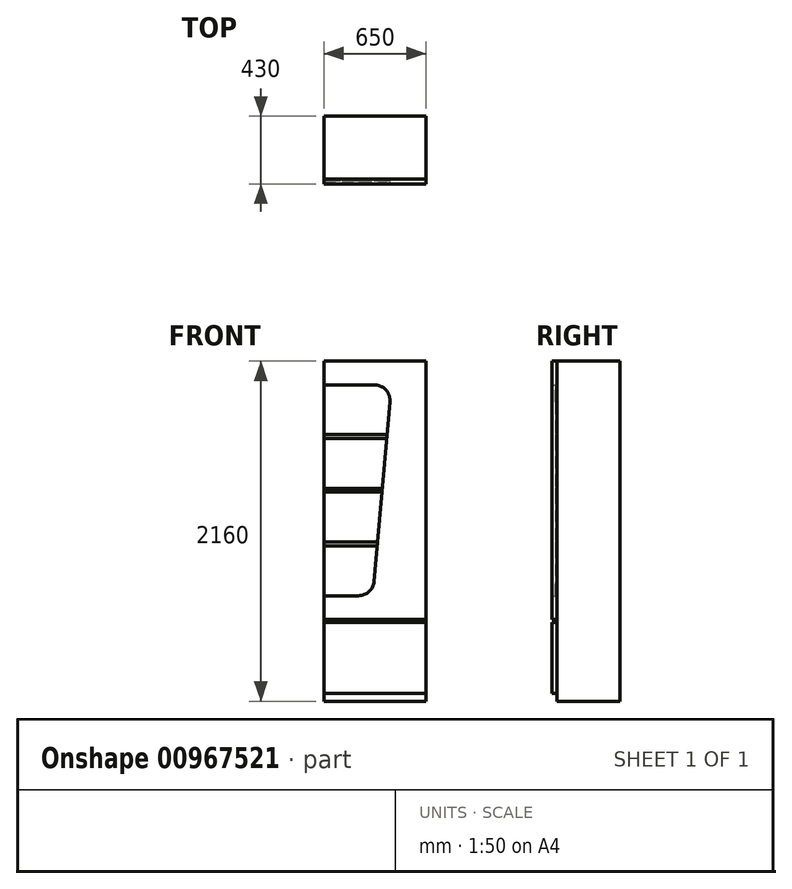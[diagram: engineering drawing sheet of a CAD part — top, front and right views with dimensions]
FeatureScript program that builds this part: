
annotation { "Feature Type Name" : "Feature", "Feature Type Description" : "" }
export const myFeature = defineFeature(function(context is Context, id is Id, definition is map)
    precondition{}
    {
        {
            assignVariable(context, id + "F0", {"variableType" : VariableType.LENGTH, "name" : "H", "lengthValue" : 2200 * mm});
        }
        {
            var Q0;
            Q0=qCreatedBy(makeId("Top.planeOp"),FACE);
            var sketch = newSketch(context, id + "F1", { "sketchPlane" : qUnion([Q0])});
            skLineSegment(sketch, "E0.bottom", {"start": v(0, 0) * mm, "end": v(650, 0) * mm});
            skLineSegment(sketch, "E0.top", {"start": v(0, 400) * mm, "end": v(650, 400) * mm});
            skLineSegment(sketch, "E0.left", {"start": v(0, 0) * mm, "end": v(0, 400) * mm});
            skLineSegment(sketch, "E0.right", {"start": v(650, 0) * mm, "end": v(650, 400) * mm});
            skSolve(sketch);
        }
        {
            var Q0;
            Q0 = qSketchRegion(id + "F1", true);
            extrude(context, id + "F2", {"entities" : qUnion([Q0]), "depth" : getVariable(context, 'H') - 40 * mm, "offsetDistance" : 25 * mm});
        }
        {
            var Q0;
            Q0=makeQuery(id+"F2.opExtrude","SWEPT_FACE",FACE,{"disambiguationData":[OSD([sQuery(id+"F1.wireOp",EDGE,"E0.bottom")])]});
            var sketch = newSketch(context, id + "F3", { "sketchPlane" : qUnion([Q0])});
            skLineSegment(sketch, "E1.bottom", {"start": v(0, 500) * mm, "end": v(650, 500) * mm});
            skLineSegment(sketch, "E1.top", {"start": v(0, 50) * mm, "end": v(650, 50) * mm});
            skLineSegment(sketch, "E1.left", {"start": v(0, 500) * mm, "end": v(0, 50) * mm});
            skLineSegment(sketch, "E1.right", {"start": v(650, 500) * mm, "end": v(650, 50) * mm});
            skLineSegment(sketch, "E2.bottom", {"start": v(0, 2160) * mm, "end": v(650, 2160) * mm});
            skLineSegment(sketch, "E2.top", {"start": v(0, 520) * mm, "end": v(650, 520) * mm});
            skLineSegment(sketch, "E2.left", {"start": v(0, 2160) * mm, "end": v(0, 520) * mm});
            skLineSegment(sketch, "E2.right", {"start": v(650, 2160) * mm, "end": v(650, 520) * mm});
            skLineSegment(sketch, "E3", {"start": v(0, 2010) * mm, "end": v(319.87, 2010) * mm});
            skLineSegment(sketch, "E4", {"start": v(419.49, 1901.28) * mm, "end": v(319.75, 761.28) * mm});
            skLineSegment(sketch, "E5", {"start": v(220.13, 670) * mm, "end": v(0, 670) * mm});
            skPoint(sketch, "E6.visualSharp", {"position": v(429, 2010) * mm});
            skArc(sketch, "E6.filletArc", {"start": v(419.49, 1901.28) * mm, "mid": v(393.6, 1977.56) * mm, "end": v(319.87, 2010) * mm});
            skPoint(sketch, "E7.visualSharp", {"position": v(311.77, 670) * mm});
            skArc(sketch, "E7.filletArc", {"start": v(220.13, 670) * mm, "mid": v(287.7, 696.27) * mm, "end": v(319.75, 761.28) * mm});
            skLineSegment(sketch, "E8", {"start": v(0, 1693.75) * mm, "end": v(401.33, 1693.75) * mm});
            skLineSegment(sketch, "E9", {"start": v(0, 1668.75) * mm, "end": v(399.14, 1668.75) * mm});
            skLineSegment(sketch, "E10.0.1.0", {"start": v(0, 1352.5) * mm, "end": v(371.48, 1352.5) * mm});
            skLineSegment(sketch, "E10.0.1.1", {"start": v(0, 1327.5) * mm, "end": v(369.29, 1327.5) * mm});
            skLineSegment(sketch, "E10.0.2.0", {"start": v(0, 1011.25) * mm, "end": v(341.62, 1011.25) * mm});
            skLineSegment(sketch, "E10.0.2.1", {"start": v(0, 986.25) * mm, "end": v(339.43, 986.25) * mm});
            skLineSegment(sketch, "E11", {"start": v(0, 1693.75) * mm, "end": v(0, 1668.75) * mm, "construction": true});
            skLineSegment(sketch, "E12", {"start": v(0, 1668.75) * mm, "end": v(0, 1352.5) * mm, "construction": true});
            skLineSegment(sketch, "E13", {"start": v(0, 1352.5) * mm, "end": v(0, 1327.5) * mm, "construction": true});
            skLineSegment(sketch, "E14", {"start": v(0, 1327.5) * mm, "end": v(0, 1011.25) * mm, "construction": true});
            skLineSegment(sketch, "E15", {"start": v(0, 1011.25) * mm, "end": v(0, 986.25) * mm, "construction": true});
            skLineSegment(sketch, "E16", {"start": v(0, 2010) * mm, "end": v(0, 1693.75) * mm, "construction": true});
            skLineSegment(sketch, "E17", {"start": v(0, 986.25) * mm, "end": v(0, 670) * mm, "construction": true});
            skSolve(sketch);
        }
        {
            var Q0;
            Q0=makeQuery(id+"F3.imprint","IMPRINT",FACE,{"disambiguationData":[TD([[makeQuery(id+"F3.imprint","IMPRINT",EDGE,{"derivedFrom":sQuery(id+"F3.wireOp",EDGE,"E1.bottom")}),-1.0]])]});
            var Q1;
            {var subQ5=sQuery(id+"F3.wireOp",EDGE,"E2.bottom");Q1=makeQuery(id+"F3.imprint","IMPRINT",FACE,{"disambiguationData":[TD([[makeQuery(id+"F3.imprint","IMPRINT",EDGE,{"derivedFrom":subQ5}),-1.0]])]});}
            extrude(context, id + "F4", {"entities" : qUnion([Q0, Q1]), "depth" : 30 * mm, "offsetDistance" : 25 * mm});
        }
        {
            var Q0;
            {var subQ1=sQuery(id+"F3.wireOp",EDGE,"E3");Q0=makeQuery(id+"F3.imprint","IMPRINT",FACE,{"disambiguationData":[TD([[makeQuery(id+"F3.imprint","IMPRINT",EDGE,{"derivedFrom":subQ1}),-1.0]])]});}
            var Q1;
            {var subQ0=sQuery(id+"F3.wireOp",EDGE,"E9");Q1=makeQuery(id+"F3.imprint","IMPRINT",FACE,{"disambiguationData":[TD([[makeQuery(id+"F3.imprint","IMPRINT",EDGE,{"derivedFrom":subQ0}),-1.0]])]});}
            var Q2;
            {var subQ0=sQuery(id+"F3.wireOp",EDGE,"E10.0.1.1");Q2=makeQuery(id+"F3.imprint","IMPRINT",FACE,{"disambiguationData":[TD([[makeQuery(id+"F3.imprint","IMPRINT",EDGE,{"derivedFrom":subQ0}),-1.0]])]});}
            var Q3;
            {var subQ1=sQuery(id+"F3.wireOp",EDGE,"E5");Q3=makeQuery(id+"F3.imprint","IMPRINT",FACE,{"disambiguationData":[TD([[makeQuery(id+"F3.imprint","IMPRINT",EDGE,{"derivedFrom":subQ1}),-1.0]])]});}
            extrude(context, id + "F5", {"entities" : qUnion([Q0, Q1, Q2, Q3]), "depth" : 10 * mm, "offsetDistance" : 25 * mm});
        }
        {
            var Q0;
            {var subQ0=sQuery(id+"F3.wireOp",EDGE,"E8");Q0=makeQuery(id+"F3.imprint","IMPRINT",FACE,{"disambiguationData":[TD([[makeQuery(id+"F3.imprint","IMPRINT",EDGE,{"derivedFrom":subQ0}),-1.0]])]});}
            var Q1;
            {var subQ0=sQuery(id+"F3.wireOp",EDGE,"E10.0.1.0");Q1=makeQuery(id+"F3.imprint","IMPRINT",FACE,{"disambiguationData":[TD([[makeQuery(id+"F3.imprint","IMPRINT",EDGE,{"derivedFrom":subQ0}),-1.0]])]});}
            var Q2;
            {var subQ0=sQuery(id+"F3.wireOp",EDGE,"E10.0.2.0");Q2=makeQuery(id+"F3.imprint","IMPRINT",FACE,{"disambiguationData":[TD([[makeQuery(id+"F3.imprint","IMPRINT",EDGE,{"derivedFrom":subQ0}),-1.0]])]});}
            extrude(context, id + "F6", {"entities" : qUnion([Q0, Q1, Q2]), "depth" : 10 * mm, "offsetDistance" : 25 * mm});
        }
    });
